# Revit family: Table-Teknion-CWTP_C-D_Conference_Extended_Knife_Edge_Power-R2016
name_source: partatom
category: Furniture
revit_build: Autodesk Revit 2018 (Build: 20190510_1515(x64)
units: mm (PartAtom-declared; Revit-internal decimal feet)

## family parameters
Always vertical = Yes
Cut with Voids When Loaded = No
OmniClass Number = 23.40.20.00
OmniClass Title = General Furniture and Specialties
Room Calculation Point = No
Shared = Yes
Work Plane-Based = No

## types (5) — shared parameters
Assembly Code = E2020200
For Additional Finishes, please visit = https://assets.teknion.com
Infill Finish = Veneer - Teknion - VM - Sisal
Leg Exterior Finish = Veneer - Teknion - VM - Sisal
Leg Exterior Finish Note = Pick a Veneer below that matches the color of the Leg Metal Finish.
Leg Metal Finish = Paint - Teknion - Mica - Anthracite
Manufacturer = Teknion
Manufacturer Fax = 416.661.4586
Part Number = CWTP
Product Documentation Link = https://assets.teknion.com
Product Line = C+D
Product Page URL = https://www.teknion.com
Series = Custom Wood
Sustainability Data = https://www.teknion.com
To render, please download texture images found here = https://assets.teknion.com
URL = www.teknion.com
Unit Weight URL = http://www.teknion.com
Warranty = http://www.teknion.com
Wood Edge Finish = Veneer - Teknion - VM - Sisal
Wood Edge Finish Note = Pick a Veneer below that matches the color of the Metal Leg.

## per-type parameters (varying)
| type | Description | Model | Outer Glass | Top Finish | Top Finish Note |
| Has Veneer Top | Custom Wood C+D Conference Table, Extended Knife Edge Power, Wood Top Material, Veneer Top | CWTP_W___ | Glass - Teknion - CL - Clear | Veneer - Teknion - VM - Sisal | Choose a Veneer Finish. |
| Has White Solid Surface Top | Custom Wood C+D Conference Table, Extended Knife Edge Power, Solid Surface Top Material, White Solid Surface | CWTP_S___ | Glass - Teknion - CL - Clear | Wood - Teknion - MV - Solid Surface - Glacier White | Choose MV Glacier White. |
| Has Grey Solid Surface Top | Custom Wood C+D Conference Table, Extended Knife Edge Power, Solid Surface Top Material, Grey Solid Surface | CWTP_S___ | Glass - Teknion - CL - Clear | Wood - Teknion - MH - Solid Surface - Stratus | Choose MH Stratus or MM Elegant Grey. |
| Has Backpainted Glass | Custom Wood C+D Conference Table, Extended Knife Edge Power, Glass Top Material, Backpainted Glass | CWTP_G___ | Glass - Teknion - CL - Clear | Back-painted Glass - K7 - Teknion - Very White | Choose a Backpainted Glass Finish. |
| Has Etched Backpainted Glass | Custom Wood C+D Conference Table, Extended Knife Edge Power, Glass Top Material, Etched Backpainted Glass | CWTP_G___ | Glass - Teknion - Low Iron Etched | Etched Back-painted Glass - HB - Teknion - Very White | Choose a Etched Backpainted Glass Finish. |

type visibility flags (boolean, named after types; folded from table):
- Has Veneer Top: Yes: Has Veneer Top
- Has White Solid Surface Top: Yes: Has White Solid Surface Top
- Has Grey Solid Surface Top: Yes: Has Grey Solid Surface Top
- Has Backpainted Glass: Yes: Has Backpainted Glass Top
- Has Etched Backpainted Glass: Yes: Has Etched Backpainted Glass Top

## geometry (parser evidence)
native form markers: Blend x41, Sweep x11
no freeform markers — native parametric forms only
